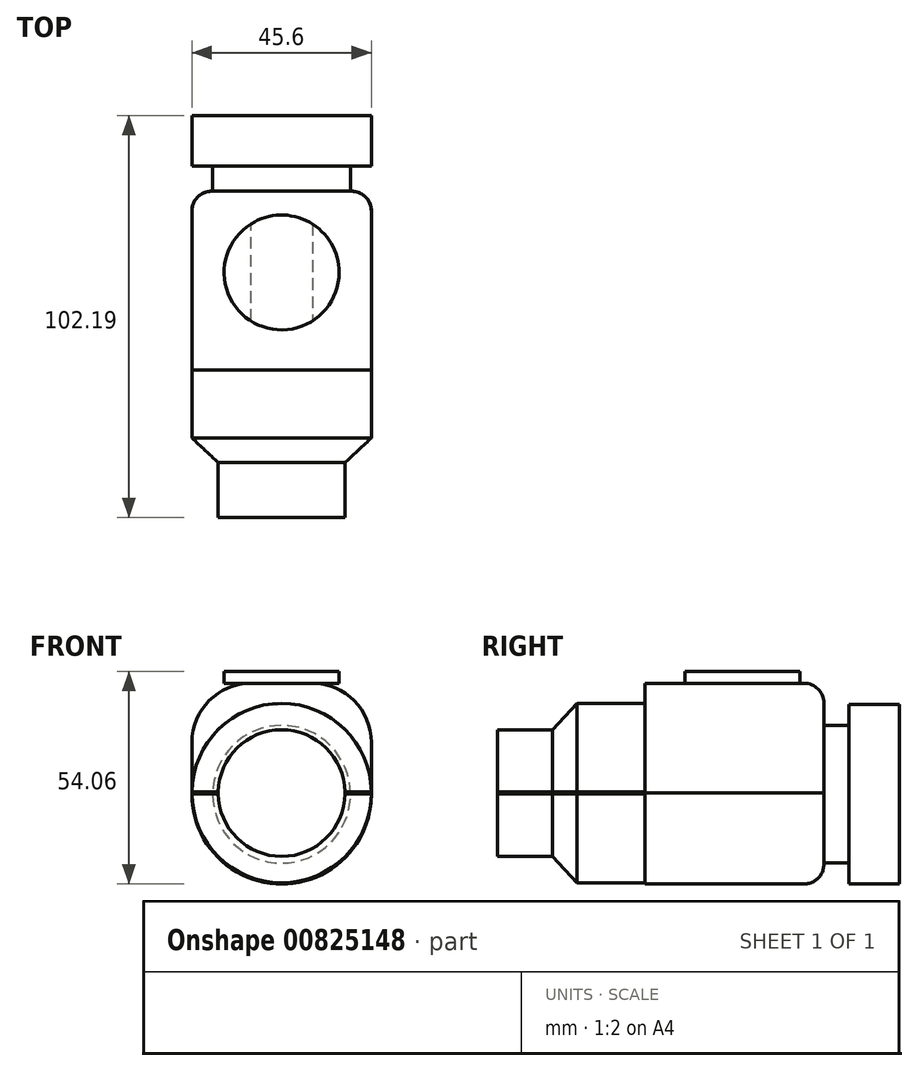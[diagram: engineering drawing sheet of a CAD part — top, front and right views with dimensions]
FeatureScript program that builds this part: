
annotation { "Feature Type Name" : "Feature", "Feature Type Description" : "" }
export const myFeature = defineFeature(function(context is Context, id is Id, definition is map)
    precondition{}
    {
        {
            var Q0;
            Q0=qCreatedBy(makeId("Front.planeOp"),FACE);
            var sketch = newSketch(context, id + "F0", { "sketchPlane" : qUnion([Q0])});
            skCircle(sketch, "E0", {"center": v(-23.65, 11.82) * mm, "radius": 22.8 * mm});
            skSolve(sketch);
        }
        {
            var Q0;
            Q0=makeQuery(id+"F0.imprint","IMPRINT",FACE,{"disambiguationData":[TD([[makeQuery(id+"F0.imprint","IMPRINT",EDGE,{"derivedFrom":sQuery(id+"F0.wireOp",EDGE,"E0")}),1.0]])]});
            extrude(context, id + "F1", {"entities" : qUnion([Q0]), "depth" : 12.8 * mm, "offsetDistance" : 25 * mm});
        }
        {
            var Q0;
            Q0=makeQuery(id+"F1.opExtrude","CAP_FACE",FACE,{"disambiguationData":[OSD([sQuery(id+"F0.wireOp",EDGE,"E0")])],"isStart":false});
            var sketch = newSketch(context, id + "F2", { "sketchPlane" : qUnion([Q0])});
            skCircle(sketch, "E1", {"center": v(-23.65, 11.82) * mm, "radius": 17.5 * mm});
            skSolve(sketch);
        }
        {
            var Q0;
            Q0=makeQuery(id+"F2.imprint","IMPRINT",FACE,{"disambiguationData":[TD([[makeQuery(id+"F2.imprint","IMPRINT",EDGE,{"derivedFrom":sQuery(id+"F2.wireOp",EDGE,"E1")}),1.0]])]});
            extrude(context, id + "F3", {"entities" : qUnion([Q0]), "operationType" : NewBodyOperationType.ADD, "depth" : 6.44 * mm, "offsetDistance" : 25 * mm});
        }
        {
            var Q0;
            Q0=makeQuery(id+"F3.opExtrude","CAP_FACE",FACE,{"disambiguationData":[OSD([sQuery(id+"F2.wireOp",EDGE,"E1")])],"isStart":false});
            var sketch = newSketch(context, id + "F4", { "sketchPlane" : qUnion([Q0])});
            skCircle(sketch, "E2", {"center": v(-23.65, 11.82) * mm, "radius": 22.8 * mm});
            skLineSegment(sketch, "E3", {"start": v(-23.65, -10.98) * mm, "end": v(-23.65, 40.02) * mm, "construction": true});
            skLineSegment(sketch, "E4.bottom", {"start": v(-46.44, 12.17) * mm, "end": v(-0.85, 12.17) * mm});
            skLineSegment(sketch, "E4.top", {"start": v(-46.44, 40.02) * mm, "end": v(-0.85, 40.02) * mm});
            skLineSegment(sketch, "E4.left", {"start": v(-46.44, 12.17) * mm, "end": v(-46.44, 40.02) * mm});
            skLineSegment(sketch, "E4.right", {"start": v(-0.85, 12.17) * mm, "end": v(-0.85, 40.02) * mm});
            skPoint(sketch, "E4.middle", {"position": v(-23.65, 40.02) * mm});
            skSolve(sketch);
        }
        {
            var Q0;
            Q0=makeQuery(id+"F4.imprint","IMPRINT",FACE,{"disambiguationData":[TD([[makeQuery(id+"F4.imprint","IMPRINT",EDGE,{"derivedFrom":makeQuery(id+"F3.opExtrude","CAP_EDGE",EDGE,{"disambiguationData":[OSD([sQuery(id+"F2.wireOp",EDGE,"E1")])],"isStart":false})}),1.0]])]});
            var Q1;
            Q1=makeQuery(id+"F4.imprint","IMPRINT",FACE,{"disambiguationData":[TD([[makeQuery(id+"F4.imprint","IMPRINT",EDGE,{"derivedFrom":sQuery(id+"F4.wireOp",EDGE,"E2")}),1.0]])]});
            var Q2;
            Q2=makeQuery(id+"F4.imprint","IMPRINT",FACE,{"disambiguationData":[TD([[makeQuery(id+"F4.imprint","IMPRINT",EDGE,{"derivedFrom":sQuery(id+"F4.wireOp",EDGE,"E4.top")}),-1.0]])]});
            extrude(context, id + "F5", {"entities" : qUnion([Q0, Q1, Q2]), "operationType" : NewBodyOperationType.ADD, "depth" : 45.4 * mm, "offsetDistance" : 25 * mm});
        }
        {
            var Q0;
            Q0=makeQuery(id+"F5.opExtrude","SWEPT_EDGE",EDGE,{"disambiguationData":[OSD([sQuery(id+"F4.wireOp",EDGE,"E4.top"),sQuery(id+"F4.wireOp",EDGE,"E4.left")])]});
            var Q1;
            Q1=makeQuery(id+"F5.opExtrude","SWEPT_EDGE",EDGE,{"disambiguationData":[OSD([sQuery(id+"F4.wireOp",EDGE,"E4.top"),sQuery(id+"F4.wireOp",EDGE,"E4.right")])]});
            fillet(context, id + "F6", {"entities" : qUnion([Q0, Q1]), "radius" : 15 * mm, "tangentPropagation" : true, "allowEdgeOverflow" : false});
        }
        {
            var Q0;
            {var subQ0=sQuery(id+"F4.wireOp",EDGE,"E4.left");var subQ1=sQuery(id+"F4.wireOp",EDGE,"E4.top");Q0=makeQuery(id+"F6.opFillet","BLEND_EDGE",EDGE,{"blendedFrom":[makeQuery(id+"F5.opExtrude","SWEPT_EDGE",EDGE,{"disambiguationData":[OSD([subQ1,subQ0])]}),makeQuery(id+"F5.opExtrude","CAP_FACE",FACE,{"disambiguationData":[OSD([sQuery(id+"F4.wireOp",EDGE,"E2"),subQ1,subQ0,sQuery(id+"F4.wireOp",EDGE,"E4.right")])],"isStart":true})],"blendedInto":[makeQuery(id+"F5.opExtrude","CAP_FACE",FACE,{"disambiguationData":[OSD([sQuery(id+"F4.wireOp",EDGE,"E2"),subQ1,subQ0,sQuery(id+"F4.wireOp",EDGE,"E4.right")])],"isStart":true})]});}
            fillet(context, id + "F7", {"entities" : qUnion([Q0]), "radius" : 5 * mm, "tangentPropagation" : true, "allowEdgeOverflow" : false});
        }
        {
            var Q0;
            Q0=makeQuery(id+"F5.opExtrude","CAP_FACE",FACE,{"disambiguationData":[OSD([sQuery(id+"F4.wireOp",EDGE,"E2"),sQuery(id+"F4.wireOp",EDGE,"E4.top"),sQuery(id+"F4.wireOp",EDGE,"E4.left"),sQuery(id+"F4.wireOp",EDGE,"E4.right")])],"isStart":false});
            var sketch = newSketch(context, id + "F8", { "sketchPlane" : qUnion([Q0])});
            skCircle(sketch, "E5", {"center": v(-23.65, 12.12) * mm, "radius": 22.8 * mm});
            skLineSegment(sketch, "E6", {"start": v(-40.94, 12.12) * mm, "end": v(-6.35, 12.12) * mm, "construction": true});
            skSolve(sketch);
        }
        {
            var Q0;
            {var subQ0=sQuery(id+"F4.wireOp",EDGE,"E4.right");var subQ1=sQuery(id+"F4.wireOp",EDGE,"E4.left");var subQ2=sQuery(id+"F4.wireOp",EDGE,"E4.top");var subQ3=sQuery(id+"F4.wireOp",EDGE,"E2");var subQ4=makeQuery(id+"F5.opExtrude","CAP_FACE",FACE,{"disambiguationData":[OSD([subQ3,subQ2,subQ1,subQ0])],"isStart":false});var subQ5=subQ4;Q0=makeQuery(id+"F8.imprint","IMPRINT",FACE,{"disambiguationData":[TD([[makeQuery(id+"F8.imprint","IMPRINT",EDGE,{"derivedFrom":makeQuery(id+"F7.opFillet","BLEND_EDGE",EDGE,{"blendedFrom":[makeQuery(id+"F5.opExtrude","CAP_EDGE",EDGE,{"disambiguationData":[OSD([subQ3])],"isStart":false}),subQ5],"blendedInto":[subQ5]})}),1.0]])]});}
            var Q1;
            {var subQ3=sQuery(id+"F8.wireOp",EDGE,"E5");var subQ5=makeQuery(id+"F5.opExtrude","CAP_EDGE",EDGE,{"disambiguationData":[OSD([sQuery(id+"F4.wireOp",EDGE,"E4.left")])],"isStart":false});var subQ9=makeQuery(id+"F8.imprint","INTERSECT",VERTEX,{"derivedFrom":[subQ5,subQ3]});Q1=makeQuery(id+"F8.imprint","IMPRINT",FACE,{"disambiguationData":[TD([[makeQuery(id+"F8.imprint","IMPRINT",EDGE,{"disambiguationData":[TD([[subQ9,1.0]])],"derivedFrom":subQ3}),1.0]])]});}
            extrude(context, id + "F9", {"entities" : qUnion([Q0, Q1]), "operationType" : NewBodyOperationType.ADD, "depth" : 17.3 * mm, "offsetDistance" : 25 * mm});
        }
        {
            var Q0;
            Q0=makeQuery(id+"F9.opExtrude","CAP_FACE",FACE,{"disambiguationData":[OSD([sQuery(id+"F8.wireOp",EDGE,"E5")])],"isStart":false});
            extrude(context, id + "F10", {"entities" : qUnion([Q0]), "operationType" : NewBodyOperationType.ADD, "depth" : 6.25 * mm, "offsetDistance" : 25 * mm, "hasDraft" : true, "draftAngle" : 47 * degree, "draftPullDirection" : true});
        }
        {
            var Q0;
            Q0=makeQuery(id+"F10.opExtrude","CAP_FACE",FACE,{"disambiguationData":[OSD([sQuery(id+"F8.wireOp",EDGE,"E5")])],"isStart":false});
            extrude(context, id + "F11", {"entities" : qUnion([Q0]), "operationType" : NewBodyOperationType.ADD, "depth" : 14 * mm, "offsetDistance" : 25 * mm});
        }
        {
            var Q0;
            Q0=makeQuery(id+"F5.opExtrude","SWEPT_FACE",FACE,{"disambiguationData":[OSD([sQuery(id+"F4.wireOp",EDGE,"E4.top")])]});
            var sketch = newSketch(context, id + "F12", { "sketchPlane" : qUnion([Q0])});
            skCircle(sketch, "E7", {"center": v(-23.65, -39.88) * mm, "radius": 14.6 * mm});
            skPoint(sketch, "E7.centerSnap0", {"position": v(-23.65, -24.24) * mm});
            skSolve(sketch);
        }
        {
            var Q0;
            Q0 = qSketchRegion(id + "F12", true);
            extrude(context, id + "F13", {"entities" : qUnion([Q0]), "operationType" : NewBodyOperationType.ADD, "depth" : 3.06 * mm, "offsetDistance" : 25 * mm});
        }
    });
